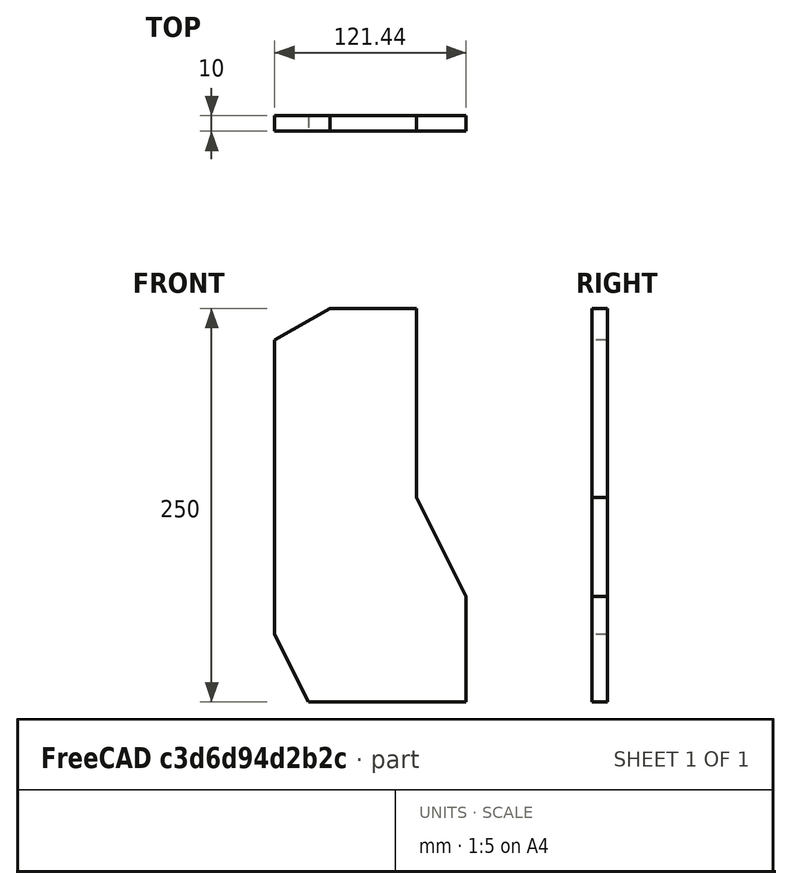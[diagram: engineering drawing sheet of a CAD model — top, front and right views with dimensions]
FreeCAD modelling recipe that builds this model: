
FCSTD DOCUMENT
Label: Y_SZ_R
objects: Sketcher::SketchObject×1, PartDesign::Pad×1
note: 3 computed .brp shape members not serialized (recipe doc carries the construction recipe); baked Part::Feature solids carry a one-line shape summary decoded from their .brp

FEATURE [Sketcher::SketchObject] Sketch
  Placement = pos=(0,0,0) rot=(1,0,0;1.5708rad)
  sketch-geometry (8):
    g0: LineSegment StartX=0 StartY=0 StartZ=0 EndX=100 EndY=0 EndZ=0
    g1: LineSegment StartX=100 StartY=0 StartZ=0 EndX=100 EndY=66.9431 EndZ=0
    g2: LineSegment StartX=100 StartY=66.9431 StartZ=0 EndX=68.561 EndY=130 EndZ=0
    g3: LineSegment StartX=68.561 StartY=130 StartZ=0 EndX=68.561 EndY=250 EndZ=0
    g4: LineSegment StartX=68.561 StartY=250 StartZ=0 EndX=13.561 EndY=250 EndZ=0
    g5: LineSegment StartX=13.561 StartY=250 StartZ=0 EndX=-21.439 EndY=229.793 EndZ=0
    g6: LineSegment StartX=-21.439 StartY=229.793 StartZ=0 EndX=-21.439 EndY=43 EndZ=0
    g7: LineSegment StartX=-21.439 StartY=43 StartZ=0 EndX=0 EndY=0 EndZ=0
  constraints (23):
    c: Horizontal(g0)
    c: Coincident(g0,g1)
    c: Vertical(g1)
    c: Coincident(g1,g2)
    c: Coincident(g2,g3)
    c: Vertical(g3)
    c: Coincident(g3,g4)
    c: Horizontal(g4)
    c: Coincident(g4,g5)
    c: Coincident(g5,g6)
    c: Coincident(g6,g7)
    c: Coincident(g7,g-1)
    c: DistanceX(g0) = 100
    c: Coincident(g0,g-1)
    c: Parallel(g2,g7)
    c: DistanceX(g5,g3) = 90
    c: DistanceY(g3) = 120
    c: DistanceY(g3,g0) = -250
    c: Vertical(g6)
    c: Angle(g2,g0) = 1.10828
    c: Angle(g6,g5) = 2.0944
    c: DistanceY(g-1,g6) = 43
    c: DistanceX(g4) = -55
FEATURE [PartDesign::Pad] Pad
  Length = 10
  Length2 = 100
  Placement = pos=(0,0,0) rot=(1,0,0;1.5708rad)
  Sketch = -> Sketch
  Type = 0
